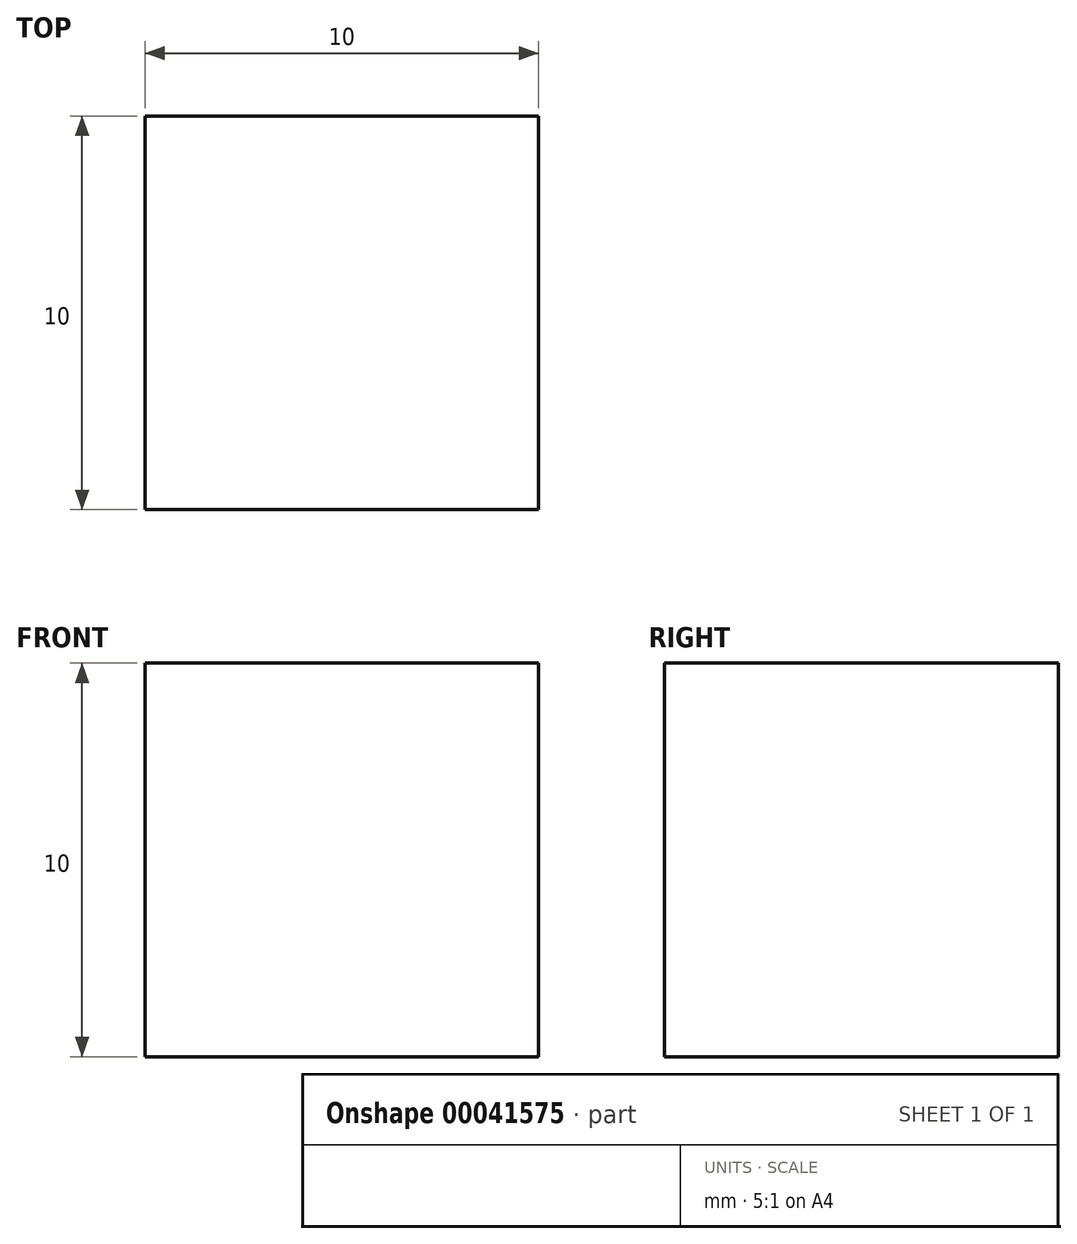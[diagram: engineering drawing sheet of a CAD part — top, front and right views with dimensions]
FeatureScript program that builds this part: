
annotation { "Feature Type Name" : "Feature", "Feature Type Description" : "" }
export const myFeature = defineFeature(function(context is Context, id is Id, definition is map)
    precondition{}
    {
        {
            var Q0;
            Q0=qCreatedBy(makeId("Top.planeOp"),FACE);
            var sketch = newSketch(context, id + "F0", { "sketchPlane" : qUnion([Q0])});
            skLineSegment(sketch, "E0.rect.bottom", {"start": v(5, -5) * mm, "end": v(-5, -5) * mm});
            skLineSegment(sketch, "E0.rect.top", {"start": v(5, 5) * mm, "end": v(-5, 5) * mm});
            skLineSegment(sketch, "E0.rect.left", {"start": v(5, -5) * mm, "end": v(5, 5) * mm});
            skLineSegment(sketch, "E0.rect.right", {"start": v(-5, -5) * mm, "end": v(-5, 5) * mm});
            skPoint(sketch, "E0.rect.middle", {"position": v(0, 0) * mm});
            skSolve(sketch);
        }
        {
            var Q0;
            Q0 = qSketchRegion(id + "F0", true);
            extrude(context, id + "F1", {"entities" : qUnion([Q0]), "depth" : 10 * mm});
        }
    });
